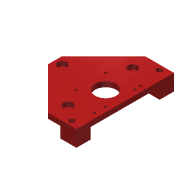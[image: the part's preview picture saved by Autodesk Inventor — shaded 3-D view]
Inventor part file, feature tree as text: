
AUTODESK INVENTOR PART (.ipt)
format: ipt  version: 2019.4 (Build 234330000, 330)  size: 247,808 bytes
history: native  units: mm
features: extrude x5, sketch x4, other x2, chamfer x1, mirror x1, projected_geometry x1, reference x1
ambient origin geometry x8: Origin, YZ Plane, XZ Plane, XY Plane, X Axis, Y Axis, Z Axis, Center Point
bodies: Solid1 (feature_tree)
feature tree (15):
  extrude  "Extrusion1"  Depth=4.9mm
  extrude  "Extrusion2"  Depth=5.5mm
  chamfer  "Chamfer1"  Distance=5.5mm
  extrude  "Extrusion4"  Depth=10.0mm TaperAngle=0.0deg
  sketch  "Sketch6"  dims[d24=10.0mm d26=6.0mm d27=0.0mm]
  extrude  "Extrusion6"  Depth=10.0mm
  mirror  "Mirror2"
  extrude  "Extrusion15"  Depth=10.0mm
  sketch  "Sketch1"  dims[d0=12.5mm d11=4.9mm]
  sketch  "Sketch4"  dims[d12=4.9mm d19=5.25mm d20=5.5mm d21=0.0mm]
  projected_geometry  "Projected Loop4"
  sketch  "Sketch16"  dims[d37=4.0mm d38=2.0mm d39=45.0deg d42=10.0mm d43=10.0mm d44=5.0mm d45=0.0mm d54=10.0mm d60=11.5mm d61=0.0mm d98=0.0mm d101=20.0mm d103=31.0mm d104=31.0mm d105=5.0mm d106=2.8mm d107=2.8mm d108=22.0mm d109=5.9mm d115=135.0deg d116=90.0deg d117=8.0mm d118=46.0mm d119=10.0mm d120=40.0mm d121=34.0mm d122=4.0mm d123=17.0mm d124=15.0mm d125=5.0mm d126=5.0mm d127=10.0mm d128=0.0mm]
  reference  "Reference1"
  other  "TOTEM_Slider_Y.iam"
  other  "Neje_Base_Slide_y_stop:1"
